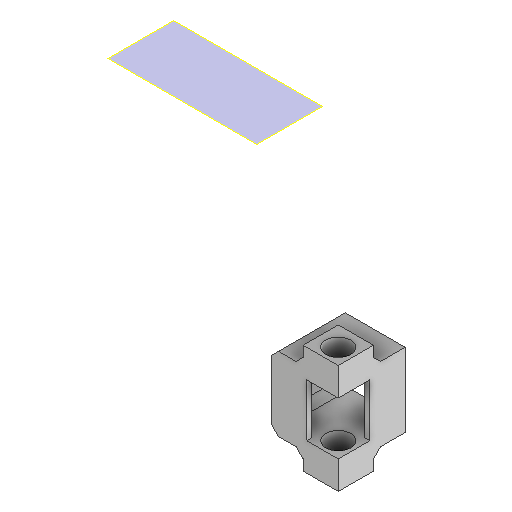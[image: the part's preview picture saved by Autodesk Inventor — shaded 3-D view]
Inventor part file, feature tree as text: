
AUTODESK INVENTOR PART (.ipt)
format: ipt  version: 2025.3 (Build 293356000, 356)  size: 184,320 bytes
history: native  units: mm
features: extrude x5, sketch x5, projected_geometry x4, other x3, plane x1, chamfer x1
ambient origin geometry x8: Origin, YZ Plane, XZ Plane, XY Plane, X Axis, Y Axis, Z Axis, Center Point
bodies: Volumenkörper1 (feature_tree)
feature tree (19):
  plane  "Arbeitsebene1"
  extrude  "Extrusion1"  Depth=19.0mm
  extrude  "Extrusion2"  Depth=19.0mm
  extrude  "Extrusion3"  Depth=3.0mm TaperAngle=0.0deg
  extrude  "Extrusion4"  Depth=3.0mm TaperAngle=0.0deg
  extrude  "Extrusion5"  Depth=9.0mm
  chamfer  "Fasen1"  Distance=9.0mm
  sketch  "Skizze1"  dims[d0=7.1mm d1=19.0mm]
  sketch  "Skizze2"  dims[d2=19.0mm d3=4.5mm]
  projected_geometry  "Projizierte Kontur1"
  sketch  "Skizze3"  dims[d4=4.5mm d5=3.0mm d6=0.0mm]
  projected_geometry  "Projizierte Kontur2"
  sketch  "Skizze4"  dims[d8=15.0mm d9=0.0mm d10=3.0mm d11=0.0mm]
  projected_geometry  "Projizierte Kontur3"
  sketch  "Skizze5"  dims[d13=1.5mm d14=9.0mm d15=9.0mm d16=10.0mm d17=10.0mm d18=5.0mm d19=0.0mm d20=10.0mm d21=10.0mm d22=5.0mm d23=0.0mm d24=2.0mm d25=2.0mm d26=45.0deg]
  projected_geometry  "Projizierte Kontur4"
  other  "<userpath>\Documents\HoLiSheet\INVENTOR\Assembly_HoliSheet_v6.iam"
  other  "Assembly_HoliSheet_v6.iam"
  other  "10_Wellplate_base_v6:1"
